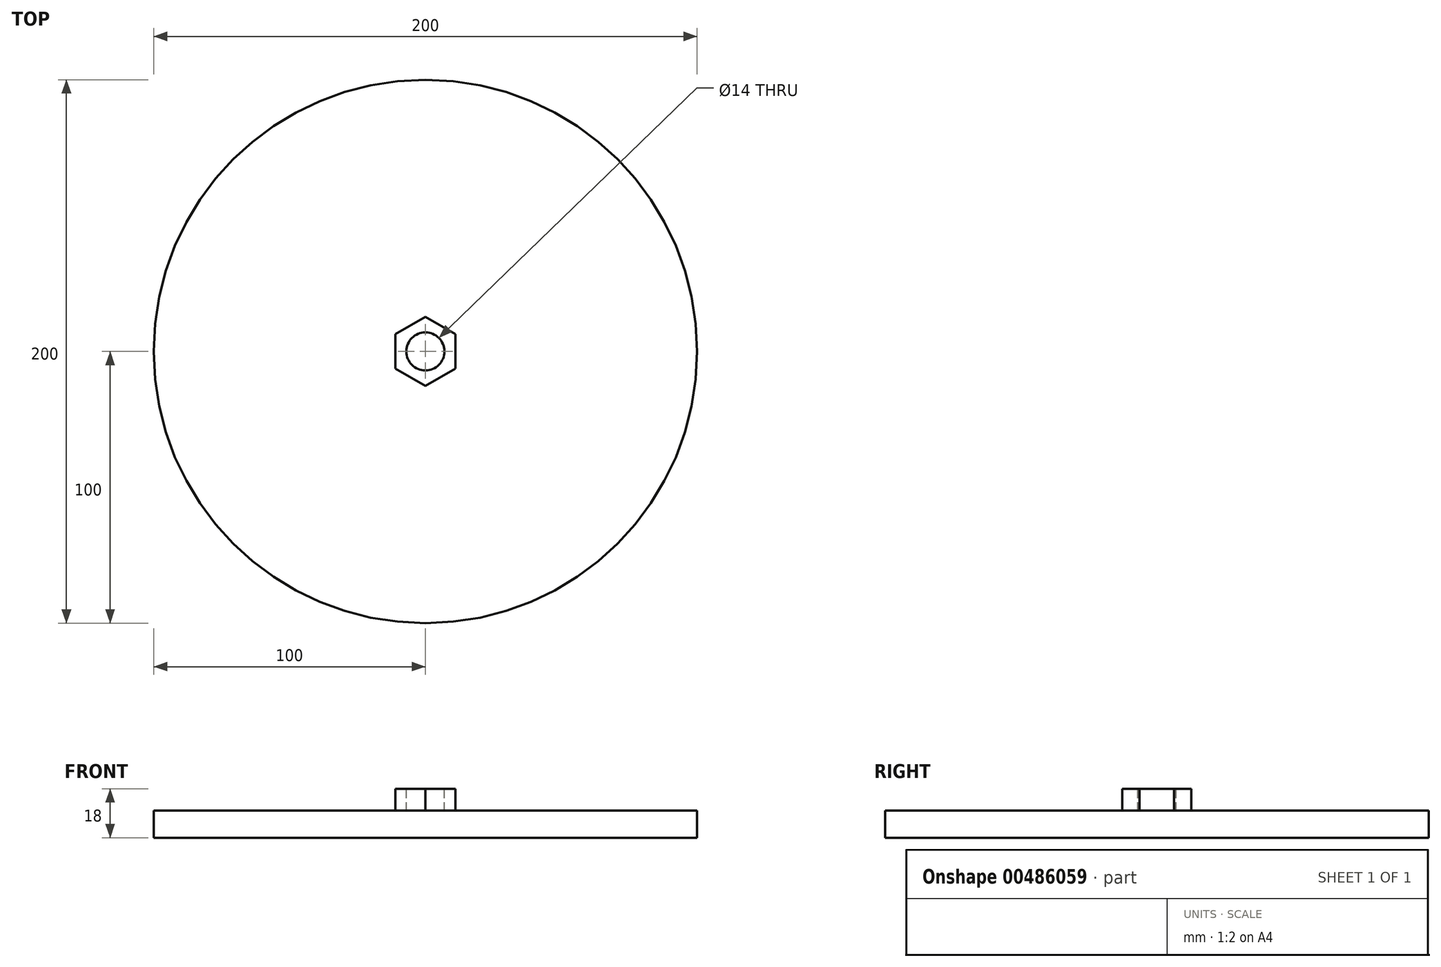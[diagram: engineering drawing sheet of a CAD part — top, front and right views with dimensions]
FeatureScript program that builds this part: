
annotation { "Feature Type Name" : "Feature", "Feature Type Description" : "" }
export const myFeature = defineFeature(function(context is Context, id is Id, definition is map)
    precondition{}
    {
        {
            var Q0;
            Q0=qCreatedBy(makeId("Top.planeOp"),FACE);
            var sketch = newSketch(context, id + "F0", { "sketchPlane" : qUnion([Q0])});
            skCircle(sketch, "E0", {"center": v(0, 0) * mm, "radius": 27.5 * mm});
            skPoint(sketch, "E1", {"position": v(17.5, 0) * mm});
            skPoint(sketch, "E2", {"position": v(0, -17.5) * mm});
            skPoint(sketch, "E3", {"position": v(-17.5, 0) * mm});
            skPoint(sketch, "E4", {"position": v(0, 17.5) * mm});
            skSolve(sketch);
        }
        {
            var Q0;
            Q0=qSketchRegion(id+"F0",true);
            extrude(context, id + "F1", {"entities" : qUnion([Q0]), "depth" : 6 * mm, "offsetDistance" : 25 * mm});
        }
        {
            var Q0;
            Q0=makeQuery(id+"F0.imprint","IMPRINT",FACE,{"disambiguationData":[TD([[makeQuery(id+"F0.imprint","IMPRINT",EDGE,{"derivedFrom":sQuery(id+"F0.wireOp",EDGE,"E0")}),1.0]])]});
            var sketch = newSketch(context, id + "F2", { "sketchPlane" : qUnion([Q0])});
            skCircle(sketch, "E5", {"center": v(0, 0) * mm, "radius": 7 * mm});
            skSolve(sketch);
        }
        {
            var Q0;
            Q0=makeQuery(id+"F2.imprint","IMPRINT",FACE,{"disambiguationData":[TD([[makeQuery(id+"F2.imprint","IMPRINT",EDGE,{"derivedFrom":sQuery(id+"F2.wireOp",EDGE,"E5")}),1.0]])]});
            extrude(context, id + "F3", {"entities" : qUnion([Q0]), "operationType" : NewBodyOperationType.ADD, "oppositeDirection" : true, "depth" : 30 * mm, "offsetDistance" : 25 * mm});
        }
        {
            var Q0;
            Q0=makeQuery(id+"F3.opExtrude","CAP_FACE",FACE,{"disambiguationData":[OSD([sQuery(id+"F2.wireOp",EDGE,"E5")])],"isStart":false});
            var sketch = newSketch(context, id + "F4", { "sketchPlane" : qUnion([Q0])});
            skCircle(sketch, "E6.cCircle", {"center": v(0, 0) * mm, "radius": 11 * mm, "construction": true});
            skLineSegment(sketch, "E6.0", {"start": v(11, 6.35) * mm, "end": v(11, -6.35) * mm});
            skLineSegment(sketch, "E6.1", {"start": v(11, -6.35) * mm, "end": v(0, -12.7) * mm});
            skLineSegment(sketch, "E6.2", {"start": v(0, -12.7) * mm, "end": v(-11, -6.35) * mm});
            skLineSegment(sketch, "E6.3", {"start": v(-11, -6.35) * mm, "end": v(-11, 6.35) * mm});
            skLineSegment(sketch, "E6.4", {"start": v(-11, 6.35) * mm, "end": v(0, 12.7) * mm});
            skLineSegment(sketch, "E6.5", {"start": v(0, 12.7) * mm, "end": v(11, 6.35) * mm});
            skPoint(sketch, "E6.0.midPoint", {"position": v(11, 0) * mm});
            skSolve(sketch);
        }
        {
            var Q0;
            Q0=makeQuery(id+"F4.imprint","IMPRINT",FACE,{"disambiguationData":[TD([[makeQuery(id+"F4.imprint","IMPRINT",EDGE,{"derivedFrom":sQuery(id+"F4.wireOp",EDGE,"E6.0")}),-1.0]])]});
            extrude(context, id + "F5", {"entities" : qUnion([Q0]), "depth" : 8 * mm, "offsetDistance" : 25 * mm});
        }
        {
            var Q0;
            Q0=makeQuery(id+"F5.opExtrude","CAP_FACE",FACE,{"disambiguationData":[OSD([sQuery(id+"F2.wireOp",EDGE,"E5"),sQuery(id+"F4.wireOp",EDGE,"E6.0"),sQuery(id+"F4.wireOp",EDGE,"E6.1"),sQuery(id+"F4.wireOp",EDGE,"E6.2"),sQuery(id+"F4.wireOp",EDGE,"E6.3"),sQuery(id+"F4.wireOp",EDGE,"E6.4"),sQuery(id+"F4.wireOp",EDGE,"E6.5")])],"isStart":false});
            var sketch = newSketch(context, id + "F6", { "sketchPlane" : qUnion([Q0])});
            skCircle(sketch, "E7", {"center": v(0, 0) * mm, "radius": 100 * mm});
            skSolve(sketch);
        }
        {
            var Q0;
            Q0=makeQuery(id+"F6.imprint","IMPRINT",FACE,{"disambiguationData":[TD([[makeQuery(id+"F6.imprint","IMPRINT",EDGE,{"derivedFrom":sQuery(id+"F6.wireOp",EDGE,"E7")}),1.0]])]});
            var Q1;
            Q1=makeQuery(id+"F6.imprint","IMPRINT",FACE,{"disambiguationData":[TD([[makeQuery(id+"F6.imprint","IMPRINT",EDGE,{"derivedFrom":makeQuery(id+"F5.opExtrude","CAP_EDGE",EDGE,{"disambiguationData":[OSD([sQuery(id+"F2.wireOp",EDGE,"E5")])],"isStart":false})}),-1.0]])]});
            var Q2;
            Q2=makeQuery(id+"F6.imprint","IMPRINT",FACE,{"disambiguationData":[TD([[makeQuery(id+"F6.imprint","IMPRINT",EDGE,{"derivedFrom":makeQuery(id+"F5.opExtrude","CAP_EDGE",EDGE,{"disambiguationData":[OSD([sQuery(id+"F4.wireOp",EDGE,"E6.0")])],"isStart":false})}),-1.0]])]});
            extrude(context, id + "F7", {"entities" : qUnion([Q0, Q1, Q2]), "depth" : 10 * mm, "offsetDistance" : 25 * mm});
        }
        {
            var Q0;
            Q0=makeQuery(id+"F1.opExtrude","SWEPT_BODY",BODY,{"disambiguationData":[OSD([sQuery(id+"F0.wireOp",EDGE,"E0")])]});
            deleteBodies(context, id + "F8", {"entities" : qUnion([Q0])});
        }
    });
